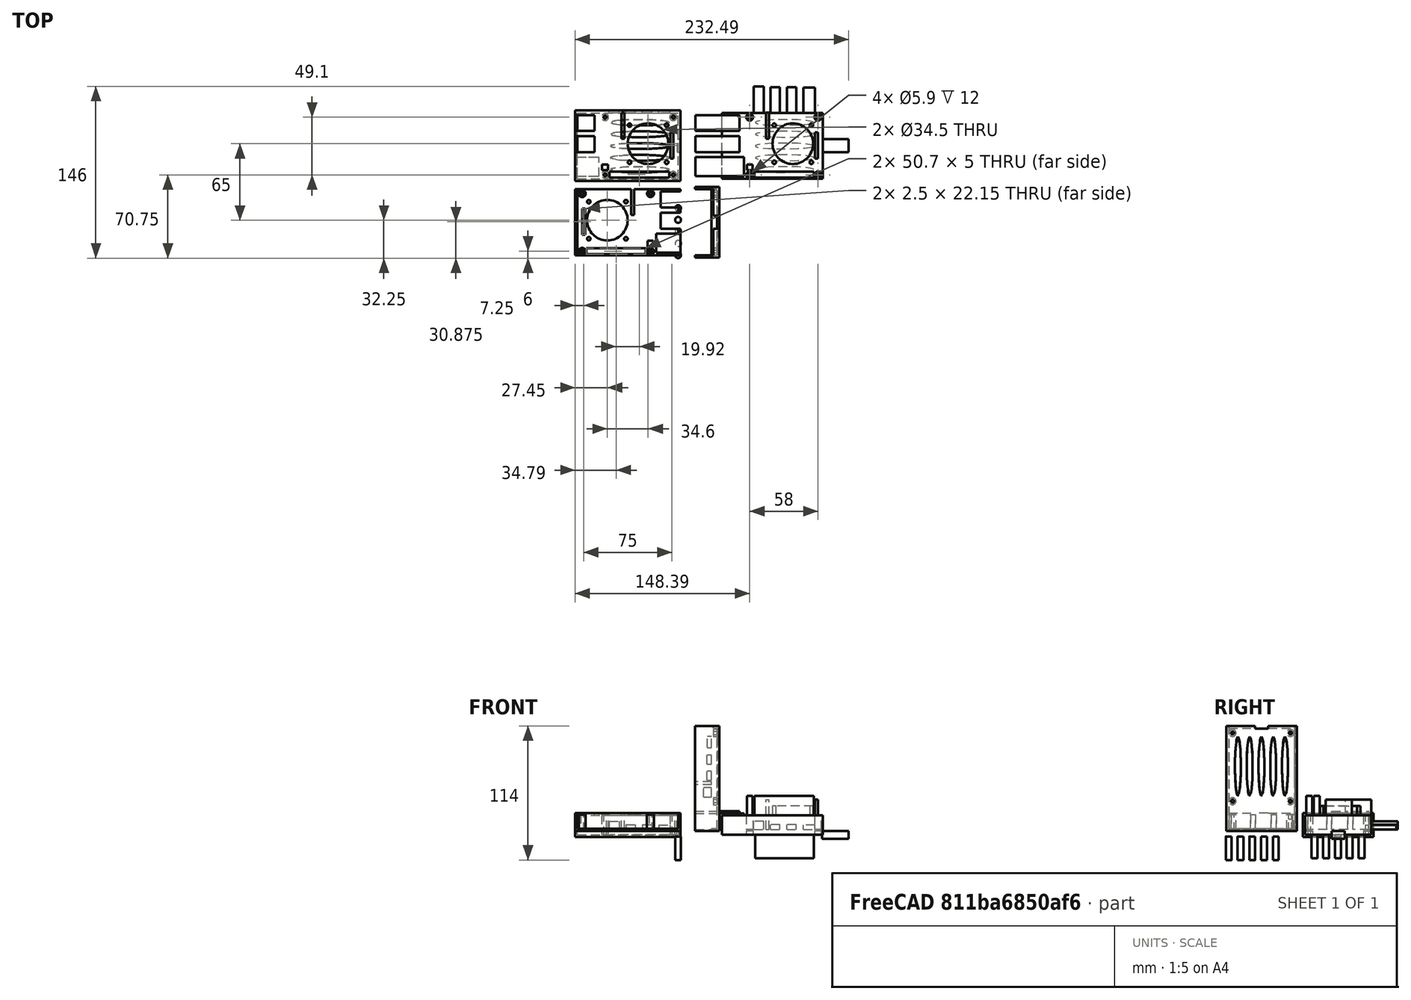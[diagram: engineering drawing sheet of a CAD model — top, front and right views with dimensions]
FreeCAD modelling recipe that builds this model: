
FCSTD DOCUMENT  (FreeCAD 0.21R33771 (Git))
Label: rpi_case_csg
License: All rights reserved
LicenseURL: http://en.wikipedia.org/wiki/All_rights_reserved
objects: Part::Cylinder×84, Part::Box×75, Part::MultiFuse×19, Part::Cut×14, Part::Fuse×7, Part::Feature×4, Part::Common×1
note: 204 computed .brp shape members not serialized (recipe doc carries the construction recipe); baked Part::Feature solids carry a one-line shape summary decoded from their .brp

FEATURE [Part::Box] cube
  AttacherType = Attacher::AttachEngine3D
  Height = 20.5
  Length = 89.5
  Placement = pos=(-2,-2,-5) rot=(0,0,1;0rad)
  Width = 60
FEATURE [Part::Box] cube001
  AttacherType = Attacher::AttachEngine3D
  Height = 1.5
  Length = 85.5
  Placement = pos=(0,0,-1.5) rot=(0,0,1;0rad)
  Width = 56
FEATURE [Part::Box] cube002
  AttacherType = Attacher::AttachEngine3D
  Height = 13.6
  Length = 41.3
  Placement = pos=(-22.81,2.15,0) rot=(0,0,1;0rad)
  Width = 16.3
FEATURE [Part::Box] cube003
  AttacherType = Attacher::AttachEngine3D
  Height = 15.6
  Length = 37.44
  Placement = pos=(-22.81,22.6,0) rot=(0,0,1;0rad)
  Width = 13.5
FEATURE [Part::Box] cube004
  AttacherType = Attacher::AttachEngine3D
  Height = 15.6
  Length = 37.44
  Placement = pos=(-22.81,40.6,0) rot=(0,0,1;0rad)
  Width = 13.5
FEATURE [Part::Box] cube005
  AttacherType = Attacher::AttachEngine3D
  Height = 28.6
  Length = 50.7
  Placement = pos=(27.36,1,0) rot=(0,0,1;0rad)
  Width = 5
FEATURE [Part::Box] cube006
  AttacherType = Attacher::AttachEngine3D
  Height = 28.6
  Length = 5
  Placement = pos=(21,7.15,0) rot=(0,0,1;0rad)
  Width = 5
FEATURE [Part::Box] cube007
  AttacherType = Attacher::AttachEngine3D
  Height = 2.5
  Length = 15
  Placement = pos=(48,16.3,0) rot=(0,0,1;0rad)
  Width = 15
FEATURE [Part::Box] cube008
  AttacherType = Attacher::AttachEngine3D
  Height = 1.8
  Length = 10.8
  Placement = pos=(67.5,6.8,0) rot=(0,0,1;0rad)
  Width = 13.1
FEATURE [Part::Box] cube009
  AttacherType = Attacher::AttachEngine3D
  Height = 25.4
  Length = 2.5
  Placement = pos=(79,17.3,0) rot=(0,0,1;0rad)
  Width = 22.15
FEATURE [Part::Box] cube010
  AttacherType = Attacher::AttachEngine3D
  Height = 3.6
  Length = 9.7
  Placement = pos=(69.1,50,0) rot=(0,0,1;0rad)
  Width = 27.4
FEATURE [Part::Box] cube011
  AttacherType = Attacher::AttachEngine3D
  Height = 3.9
  Length = 7.95
  Placement = pos=(55,50,0) rot=(0,0,1;0rad)
  Width = 27.8
FEATURE [Part::Box] cube012
  AttacherType = Attacher::AttachEngine3D
  Height = 3.9
  Length = 7.95
  Placement = pos=(41.2,50,0) rot=(0,0,1;0rad)
  Width = 27.8
FEATURE [Part::Box] cube013
  AttacherType = Attacher::AttachEngine3D
  Height = 25.4
  Length = 2.5
  Placement = pos=(37.4,34.1,0) rot=(0,0,1;0rad)
  Width = 22.15
FEATURE [Part::Box] cube014
  AttacherType = Attacher::AttachEngine3D
  Height = 6.9
  Length = 8.5
  Placement = pos=(26.9,43.55,0) rot=(0,0,1;0rad)
  Width = 34.95
FEATURE [Part::Box] cube015
  AttacherType = Attacher::AttachEngine3D
  Height = 6.5
  Length = 22.55
  Placement = pos=(85,22.4,-8) rot=(0,0,1;0rad)
  Width = 11.11
FEATURE [Part::Cylinder] cylinder
  Angle = 360
  AttacherType = Attacher::AttachEngine3D
  FirstAngle = 0
  Height = 20
  Placement = pos=(44.3,14,0) rot=(0,0,1;0rad)
  Radius = 1.5
  SecondAngle = 0
FEATURE [Part::Cylinder] cylinder001
  Angle = 360
  AttacherType = Attacher::AttachEngine3D
  FirstAngle = 0
  Height = 20
  Placement = pos=(44.3,45.5,0) rot=(0,0,1;0rad)
  Radius = 1.5
  SecondAngle = 0
FEATURE [Part::Cylinder] cylinder002
  Angle = 360
  AttacherType = Attacher::AttachEngine3D
  FirstAngle = 0
  Height = 20
  Placement = pos=(75.8,14,0) rot=(0,0,1;0rad)
  Radius = 1.5
  SecondAngle = 0
FEATURE [Part::Cylinder] cylinder003
  Angle = 360
  AttacherType = Attacher::AttachEngine3D
  FirstAngle = 0
  Height = 20
  Placement = pos=(75.8,45.5,0) rot=(0,0,1;0rad)
  Radius = 1.5
  SecondAngle = 0
FEATURE [Part::Cylinder] cylinder004
  Angle = 360
  AttacherType = Attacher::AttachEngine3D
  FirstAngle = 0
  Height = 20
  Placement = pos=(60.05,29.75,0) rot=(0,0,1;0rad)
  Radius = 17.25
  SecondAngle = 0
FEATURE [Part::Cylinder] cylinder005 .. cylinder009  x5 (patterned run collapsed; names and placements below)
  Angle = 360
  AttacherType = Attacher::AttachEngine3D
  FirstAngle = 0
  Height = 20
  Radius = 2.5
  SecondAngle = 0
  placements: 5 in arithmetic series — first pos=(0,0,-24.5) rot=(0,0,1;0rad), step (0,10,0), last pos=(0,40,-24.5) rot=(0,0,1;0rad)
FEATURE [Part::MultiFuse] Matrix_Union
  Shapes = -> [cylinder005,cylinder006,cylinder007,cylinder008,cylinder009]
FEATURE [Part::Feature] Matrix_Deformation
  Placement = pos=(53,7.8,0) rot=(0,0,1;0rad)
  shape: bbox 75 x 48.66 x 20 mm, 15 faces, 5 solids (baked)
FEATURE [Part::Box] cube016
  AttacherType = Attacher::AttachEngine3D
  Height = 12
  Length = 85.5
  Width = 56
FEATURE [Part::Box] cube017
  AttacherType = Attacher::AttachEngine3D
  Height = 3
  Length = 85.5
  Placement = pos=(0,0,-4.5) rot=(0,0,1;0rad)
  Width = 56
FEATURE [Part::Fuse] union
  Base = -> cube016
  Tool = -> cube017
FEATURE [Part::Cylinder] cylinder010
  Angle = 360
  AttacherType = Attacher::AttachEngine3D
  FirstAngle = 0
  Height = 22
  Placement = pos=(22.2,2,-11) rot=(0,0,1;0rad)
  Radius = 2.95
  SecondAngle = 0
FEATURE [Part::Cylinder] cylinder011
  Angle = 360
  AttacherType = Attacher::AttachEngine3D
  FirstAngle = 0
  Height = 22
  Placement = pos=(22.2,51.1,-11) rot=(0,0,1;0rad)
  Radius = 2.95
  SecondAngle = 0
FEATURE [Part::Cylinder] cylinder012
  Angle = 360
  AttacherType = Attacher::AttachEngine3D
  FirstAngle = 0
  Height = 22
  Placement = pos=(80.2,2,-11) rot=(0,0,1;0rad)
  Radius = 2.95
  SecondAngle = 0
FEATURE [Part::Cylinder] cylinder013
  Angle = 360
  AttacherType = Attacher::AttachEngine3D
  FirstAngle = 0
  Height = 22
  Placement = pos=(80.2,51.1,-11) rot=(0,0,1;0rad)
  Radius = 2.95
  SecondAngle = 0
FEATURE [Part::MultiFuse] Matrix_Union001
  Placement = pos=(1.25,1.25,4.5) rot=(0,0,1;0rad)
  Shapes = -> [cylinder010,cylinder011,cylinder012,cylinder013]
FEATURE [Part::Cut] difference
  Base = -> union
  Tool = -> Matrix_Union001
FEATURE [Part::MultiFuse] Matrix_Union002
  Placement = pos=(0,0,1.5) rot=(0,0,1;0rad)
  Shapes = -> [cube001,cube002,cube003,cube004,cube005,cube006,cube007,cube008,cube009,cube010,cube011,cube012,cube013,cube014,cube015,cylinder,cylinder001,cylinder002,cylinder003,cylinder004,Matrix_Deformation,difference]
FEATURE [Part::Cylinder] cylinder014
  Angle = 360
  AttacherType = Attacher::AttachEngine3D
  FirstAngle = 0
  Height = 22
  Placement = pos=(22.2,2,-11) rot=(0,0,1;0rad)
  Radius = 1.25
  SecondAngle = 0
FEATURE [Part::Cylinder] cylinder015
  Angle = 360
  AttacherType = Attacher::AttachEngine3D
  FirstAngle = 0
  Height = 22
  Placement = pos=(22.2,51.1,-11) rot=(0,0,1;0rad)
  Radius = 1.25
  SecondAngle = 0
FEATURE [Part::Cylinder] cylinder016
  Angle = 360
  AttacherType = Attacher::AttachEngine3D
  FirstAngle = 0
  Height = 22
  Placement = pos=(80.2,2,-11) rot=(0,0,1;0rad)
  Radius = 1.25
  SecondAngle = 0
FEATURE [Part::Cylinder] cylinder017
  Angle = 360
  AttacherType = Attacher::AttachEngine3D
  FirstAngle = 0
  Height = 22
  Placement = pos=(80.2,51.1,-11) rot=(0,0,1;0rad)
  Radius = 1.25
  SecondAngle = 0
FEATURE [Part::MultiFuse] Matrix_Union003
  Placement = pos=(1.25,1.25,4.5) rot=(0,0,1;0rad)
  Shapes = -> [cylinder014,cylinder015,cylinder016,cylinder017]
FEATURE [Part::Cut] difference001
  Base = -> Matrix_Union002
  Tool = -> Matrix_Union003
FEATURE [Part::Cylinder] cylinder018
  Angle = 360
  AttacherType = Attacher::AttachEngine3D
  FirstAngle = 0
  Height = 22
  Placement = pos=(22.2,2,-11) rot=(0,0,1;0rad)
  Radius = 1.25
  SecondAngle = 0
FEATURE [Part::Cylinder] cylinder019
  Angle = 360
  AttacherType = Attacher::AttachEngine3D
  FirstAngle = 0
  Height = 22
  Placement = pos=(22.2,51.1,-11) rot=(0,0,1;0rad)
  Radius = 1.25
  SecondAngle = 0
FEATURE [Part::Cylinder] cylinder020
  Angle = 360
  AttacherType = Attacher::AttachEngine3D
  FirstAngle = 0
  Height = 22
  Placement = pos=(80.2,2,-11) rot=(0,0,1;0rad)
  Radius = 1.25
  SecondAngle = 0
FEATURE [Part::Cylinder] cylinder021
  Angle = 360
  AttacherType = Attacher::AttachEngine3D
  FirstAngle = 0
  Height = 22
  Placement = pos=(80.2,51.1,-11) rot=(0,0,1;0rad)
  Radius = 1.25
  SecondAngle = 0
FEATURE [Part::MultiFuse] Matrix_Union004
  Placement = pos=(1.25,1.25,4.5) rot=(0,0,1;0rad)
  Shapes = -> [cylinder018,cylinder019,cylinder020,cylinder021]
FEATURE [Part::Fuse] union001
  Base = -> difference001
  Tool = -> Matrix_Union004
FEATURE [Part::Cut] difference002
  Base = -> cube
  Tool = -> union001
FEATURE [Part::Box] cube018
  AttacherType = Attacher::AttachEngine3D
  Height = 17
  Length = 89.5
  Placement = pos=(-2,0,0) rot=(0,0,1;0rad)
  Width = 56
FEATURE [Part::Box] cube019
  AttacherType = Attacher::AttachEngine3D
  Height = 1.5
  Length = 2
  Placement = pos=(-2,0,0) rot=(0,0,1;0rad)
  Width = 56
FEATURE [Part::Cut] difference003
  Base = -> cube018
  Tool = -> cube019
FEATURE [Part::Common] intersection
  Base = -> difference002
  Placement = pos=(0,0,15.5) rot=(0,1,0;3.14159rad)
  Tool = -> difference003
FEATURE [Part::Box] cube020
  AttacherType = Attacher::AttachEngine3D
  Height = 20.5
  Length = 89.5
  Placement = pos=(-2,-2,-5) rot=(0,0,1;0rad)
  Width = 60
FEATURE [Part::Box] cube021
  AttacherType = Attacher::AttachEngine3D
  Height = 1.5
  Length = 85.5
  Placement = pos=(0,0,-1.5) rot=(0,0,1;0rad)
  Width = 56
FEATURE [Part::Box] cube022
  AttacherType = Attacher::AttachEngine3D
  Height = 13.6
  Length = 41.3
  Placement = pos=(-22.81,2.15,0) rot=(0,0,1;0rad)
  Width = 16.3
FEATURE [Part::Box] cube023
  AttacherType = Attacher::AttachEngine3D
  Height = 15.6
  Length = 37.44
  Placement = pos=(-22.81,22.6,0) rot=(0,0,1;0rad)
  Width = 13.5
FEATURE [Part::Box] cube024
  AttacherType = Attacher::AttachEngine3D
  Height = 15.6
  Length = 37.44
  Placement = pos=(-22.81,40.6,0) rot=(0,0,1;0rad)
  Width = 13.5
FEATURE [Part::Box] cube025
  AttacherType = Attacher::AttachEngine3D
  Height = 28.6
  Length = 50.7
  Placement = pos=(27.36,1,0) rot=(0,0,1;0rad)
  Width = 5
FEATURE [Part::Box] cube026
  AttacherType = Attacher::AttachEngine3D
  Height = 28.6
  Length = 5
  Placement = pos=(21,7.15,0) rot=(0,0,1;0rad)
  Width = 5
FEATURE [Part::Box] cube027
  AttacherType = Attacher::AttachEngine3D
  Height = 2.5
  Length = 15
  Placement = pos=(48,16.3,0) rot=(0,0,1;0rad)
  Width = 15
FEATURE [Part::Box] cube028
  AttacherType = Attacher::AttachEngine3D
  Height = 1.8
  Length = 10.8
  Placement = pos=(67.5,6.8,0) rot=(0,0,1;0rad)
  Width = 13.1
FEATURE [Part::Box] cube029
  AttacherType = Attacher::AttachEngine3D
  Height = 25.4
  Length = 2.5
  Placement = pos=(79,17.3,0) rot=(0,0,1;0rad)
  Width = 22.15
FEATURE [Part::Box] cube030
  AttacherType = Attacher::AttachEngine3D
  Height = 3.6
  Length = 9.7
  Placement = pos=(69.1,50,0) rot=(0,0,1;0rad)
  Width = 27.4
FEATURE [Part::Box] cube031
  AttacherType = Attacher::AttachEngine3D
  Height = 3.9
  Length = 7.95
  Placement = pos=(55,50,0) rot=(0,0,1;0rad)
  Width = 27.8
FEATURE [Part::Box] cube032
  AttacherType = Attacher::AttachEngine3D
  Height = 3.9
  Length = 7.95
  Placement = pos=(41.2,50,0) rot=(0,0,1;0rad)
  Width = 27.8
FEATURE [Part::Box] cube033
  AttacherType = Attacher::AttachEngine3D
  Height = 25.4
  Length = 2.5
  Placement = pos=(37.4,34.1,0) rot=(0,0,1;0rad)
  Width = 22.15
FEATURE [Part::Box] cube034
  AttacherType = Attacher::AttachEngine3D
  Height = 6.9
  Length = 8.5
  Placement = pos=(26.9,43.55,0) rot=(0,0,1;0rad)
  Width = 34.95
FEATURE [Part::Box] cube035
  AttacherType = Attacher::AttachEngine3D
  Height = 6.5
  Length = 22.55
  Placement = pos=(85,22.4,-8) rot=(0,0,1;0rad)
  Width = 11.11
FEATURE [Part::Cylinder] cylinder022
  Angle = 360
  AttacherType = Attacher::AttachEngine3D
  FirstAngle = 0
  Height = 20
  Placement = pos=(44.3,14,0) rot=(0,0,1;0rad)
  Radius = 1.5
  SecondAngle = 0
FEATURE [Part::Cylinder] cylinder023
  Angle = 360
  AttacherType = Attacher::AttachEngine3D
  FirstAngle = 0
  Height = 20
  Placement = pos=(44.3,45.5,0) rot=(0,0,1;0rad)
  Radius = 1.5
  SecondAngle = 0
FEATURE [Part::Cylinder] cylinder024
  Angle = 360
  AttacherType = Attacher::AttachEngine3D
  FirstAngle = 0
  Height = 20
  Placement = pos=(75.8,14,0) rot=(0,0,1;0rad)
  Radius = 1.5
  SecondAngle = 0
FEATURE [Part::Cylinder] cylinder025
  Angle = 360
  AttacherType = Attacher::AttachEngine3D
  FirstAngle = 0
  Height = 20
  Placement = pos=(75.8,45.5,0) rot=(0,0,1;0rad)
  Radius = 1.5
  SecondAngle = 0
FEATURE [Part::Cylinder] cylinder026
  Angle = 360
  AttacherType = Attacher::AttachEngine3D
  FirstAngle = 0
  Height = 20
  Placement = pos=(60.05,29.75,0) rot=(0,0,1;0rad)
  Radius = 17.25
  SecondAngle = 0
FEATURE [Part::Cylinder] cylinder027 .. cylinder031  x5 (patterned run collapsed; names and placements below)
  Angle = 360
  AttacherType = Attacher::AttachEngine3D
  FirstAngle = 0
  Height = 20
  Radius = 2.5
  SecondAngle = 0
  placements: 5 in arithmetic series — first pos=(0,0,-24.5) rot=(0,0,1;0rad), step (0,10,0), last pos=(0,40,-24.5) rot=(0,0,1;0rad)
FEATURE [Part::MultiFuse] Matrix_Union005
  Shapes = -> [cylinder027,cylinder028,cylinder029,cylinder030,cylinder031]
FEATURE [Part::Feature] Matrix_Deformation001
  Placement = pos=(53,7.8,0) rot=(0,0,1;0rad)
  shape: bbox 75 x 48.66 x 20 mm, 15 faces, 5 solids (baked)
FEATURE [Part::Box] cube036
  AttacherType = Attacher::AttachEngine3D
  Height = 12
  Length = 85.5
  Width = 56
FEATURE [Part::Box] cube037
  AttacherType = Attacher::AttachEngine3D
  Height = 3
  Length = 85.5
  Placement = pos=(0,0,-4.5) rot=(0,0,1;0rad)
  Width = 56
FEATURE [Part::Fuse] union002
  Base = -> cube036
  Tool = -> cube037
FEATURE [Part::Cylinder] cylinder032
  Angle = 360
  AttacherType = Attacher::AttachEngine3D
  FirstAngle = 0
  Height = 22
  Placement = pos=(22.2,2,-11) rot=(0,0,1;0rad)
  Radius = 2.95
  SecondAngle = 0
FEATURE [Part::Cylinder] cylinder033
  Angle = 360
  AttacherType = Attacher::AttachEngine3D
  FirstAngle = 0
  Height = 22
  Placement = pos=(22.2,51.1,-11) rot=(0,0,1;0rad)
  Radius = 2.95
  SecondAngle = 0
FEATURE [Part::Cylinder] cylinder034
  Angle = 360
  AttacherType = Attacher::AttachEngine3D
  FirstAngle = 0
  Height = 22
  Placement = pos=(80.2,2,-11) rot=(0,0,1;0rad)
  Radius = 2.95
  SecondAngle = 0
FEATURE [Part::Cylinder] cylinder035
  Angle = 360
  AttacherType = Attacher::AttachEngine3D
  FirstAngle = 0
  Height = 22
  Placement = pos=(80.2,51.1,-11) rot=(0,0,1;0rad)
  Radius = 2.95
  SecondAngle = 0
FEATURE [Part::MultiFuse] Matrix_Union006
  Placement = pos=(1.25,1.25,4.5) rot=(0,0,1;0rad)
  Shapes = -> [cylinder032,cylinder033,cylinder034,cylinder035]
FEATURE [Part::Cut] difference004
  Base = -> union002
  Tool = -> Matrix_Union006
FEATURE [Part::MultiFuse] Matrix_Union007
  Placement = pos=(0,0,1.5) rot=(0,0,1;0rad)
  Shapes = -> [cube021,cube022,cube023,cube024,cube025,cube026,cube027,cube028,cube029,cube030,cube031,cube032,cube033,cube034,cube035,cylinder022,cylinder023,cylinder024,cylinder025,cylinder026,Matrix_Deformation001,difference004]
FEATURE [Part::Cylinder] cylinder036
  Angle = 360
  AttacherType = Attacher::AttachEngine3D
  FirstAngle = 0
  Height = 22
  Placement = pos=(22.2,2,-11) rot=(0,0,1;0rad)
  Radius = 1.25
  SecondAngle = 0
FEATURE [Part::Cylinder] cylinder037
  Angle = 360
  AttacherType = Attacher::AttachEngine3D
  FirstAngle = 0
  Height = 22
  Placement = pos=(22.2,51.1,-11) rot=(0,0,1;0rad)
  Radius = 1.25
  SecondAngle = 0
FEATURE [Part::Cylinder] cylinder038
  Angle = 360
  AttacherType = Attacher::AttachEngine3D
  FirstAngle = 0
  Height = 22
  Placement = pos=(80.2,2,-11) rot=(0,0,1;0rad)
  Radius = 1.25
  SecondAngle = 0
FEATURE [Part::Cylinder] cylinder039
  Angle = 360
  AttacherType = Attacher::AttachEngine3D
  FirstAngle = 0
  Height = 22
  Placement = pos=(80.2,51.1,-11) rot=(0,0,1;0rad)
  Radius = 1.25
  SecondAngle = 0
FEATURE [Part::MultiFuse] Matrix_Union008
  Placement = pos=(1.25,1.25,4.5) rot=(0,0,1;0rad)
  Shapes = -> [cylinder036,cylinder037,cylinder038,cylinder039]
FEATURE [Part::Cut] difference005
  Base = -> Matrix_Union007
  Tool = -> Matrix_Union008
FEATURE [Part::Cylinder] cylinder040
  Angle = 360
  AttacherType = Attacher::AttachEngine3D
  FirstAngle = 0
  Height = 22
  Placement = pos=(22.2,2,-11) rot=(0,0,1;0rad)
  Radius = 1.25
  SecondAngle = 0
FEATURE [Part::Cylinder] cylinder041
  Angle = 360
  AttacherType = Attacher::AttachEngine3D
  FirstAngle = 0
  Height = 22
  Placement = pos=(22.2,51.1,-11) rot=(0,0,1;0rad)
  Radius = 1.25
  SecondAngle = 0
FEATURE [Part::Cylinder] cylinder042
  Angle = 360
  AttacherType = Attacher::AttachEngine3D
  FirstAngle = 0
  Height = 22
  Placement = pos=(80.2,2,-11) rot=(0,0,1;0rad)
  Radius = 1.25
  SecondAngle = 0
FEATURE [Part::Cylinder] cylinder043
  Angle = 360
  AttacherType = Attacher::AttachEngine3D
  FirstAngle = 0
  Height = 22
  Placement = pos=(80.2,51.1,-11) rot=(0,0,1;0rad)
  Radius = 1.25
  SecondAngle = 0
FEATURE [Part::MultiFuse] Matrix_Union009
  Placement = pos=(1.25,1.25,4.5) rot=(0,0,1;0rad)
  Shapes = -> [cylinder040,cylinder041,cylinder042,cylinder043]
FEATURE [Part::Fuse] union003
  Base = -> difference005
  Tool = -> Matrix_Union009
FEATURE [Part::Cut] difference006
  Base = -> cube020
  Tool = -> union003
FEATURE [Part::Box] cube038
  AttacherType = Attacher::AttachEngine3D
  Height = 17
  Length = 89.5
  Placement = pos=(-2,0,0) rot=(0,0,1;0rad)
  Width = 56
FEATURE [Part::Box] cube039
  AttacherType = Attacher::AttachEngine3D
  Height = 1.5
  Length = 2
  Placement = pos=(-2,0,0) rot=(0,0,1;0rad)
  Width = 56
FEATURE [Part::Cut] difference007
  Base = -> cube038
  Tool = -> cube039
FEATURE [Part::Cut] difference008
  Base = -> difference006
  Placement = pos=(30,0,2) rot=(0,-1,0;1.5708rad)
  Tool = -> difference007
FEATURE [Part::Box] cube040
  AttacherType = Attacher::AttachEngine3D
  Height = 20.5
  Length = 89.5
  Placement = pos=(-2,-2,-5) rot=(0,0,1;0rad)
  Width = 60
FEATURE [Part::Box] cube041
  AttacherType = Attacher::AttachEngine3D
  Height = 1.5
  Length = 85.5
  Placement = pos=(0,0,-1.5) rot=(0,0,1;0rad)
  Width = 56
FEATURE [Part::Box] cube042
  AttacherType = Attacher::AttachEngine3D
  Height = 13.6
  Length = 41.3
  Placement = pos=(-22.81,2.15,0) rot=(0,0,1;0rad)
  Width = 16.3
FEATURE [Part::Box] cube043
  AttacherType = Attacher::AttachEngine3D
  Height = 15.6
  Length = 37.44
  Placement = pos=(-22.81,22.6,0) rot=(0,0,1;0rad)
  Width = 13.5
FEATURE [Part::Box] cube044
  AttacherType = Attacher::AttachEngine3D
  Height = 15.6
  Length = 37.44
  Placement = pos=(-22.81,40.6,0) rot=(0,0,1;0rad)
  Width = 13.5
FEATURE [Part::Box] cube045
  AttacherType = Attacher::AttachEngine3D
  Height = 28.6
  Length = 50.7
  Placement = pos=(27.36,1,0) rot=(0,0,1;0rad)
  Width = 5
FEATURE [Part::Box] cube046
  AttacherType = Attacher::AttachEngine3D
  Height = 28.6
  Length = 5
  Placement = pos=(21,7.15,0) rot=(0,0,1;0rad)
  Width = 5
FEATURE [Part::Box] cube047
  AttacherType = Attacher::AttachEngine3D
  Height = 2.5
  Length = 15
  Placement = pos=(48,16.3,0) rot=(0,0,1;0rad)
  Width = 15
FEATURE [Part::Box] cube048
  AttacherType = Attacher::AttachEngine3D
  Height = 1.8
  Length = 10.8
  Placement = pos=(67.5,6.8,0) rot=(0,0,1;0rad)
  Width = 13.1
FEATURE [Part::Box] cube049
  AttacherType = Attacher::AttachEngine3D
  Height = 25.4
  Length = 2.5
  Placement = pos=(79,17.3,0) rot=(0,0,1;0rad)
  Width = 22.15
FEATURE [Part::Box] cube050
  AttacherType = Attacher::AttachEngine3D
  Height = 3.6
  Length = 9.7
  Placement = pos=(69.1,50,0) rot=(0,0,1;0rad)
  Width = 27.4
FEATURE [Part::Box] cube051
  AttacherType = Attacher::AttachEngine3D
  Height = 3.9
  Length = 7.95
  Placement = pos=(55,50,0) rot=(0,0,1;0rad)
  Width = 27.8
FEATURE [Part::Box] cube052
  AttacherType = Attacher::AttachEngine3D
  Height = 3.9
  Length = 7.95
  Placement = pos=(41.2,50,0) rot=(0,0,1;0rad)
  Width = 27.8
FEATURE [Part::Box] cube053
  AttacherType = Attacher::AttachEngine3D
  Height = 25.4
  Length = 2.5
  Placement = pos=(37.4,34.1,0) rot=(0,0,1;0rad)
  Width = 22.15
FEATURE [Part::Box] cube054
  AttacherType = Attacher::AttachEngine3D
  Height = 6.9
  Length = 8.5
  Placement = pos=(26.9,43.55,0) rot=(0,0,1;0rad)
  Width = 34.95
FEATURE [Part::Box] cube055
  AttacherType = Attacher::AttachEngine3D
  Height = 6.5
  Length = 22.55
  Placement = pos=(85,22.4,-8) rot=(0,0,1;0rad)
  Width = 11.11
FEATURE [Part::Cylinder] cylinder044
  Angle = 360
  AttacherType = Attacher::AttachEngine3D
  FirstAngle = 0
  Height = 20
  Placement = pos=(44.3,14,0) rot=(0,0,1;0rad)
  Radius = 1.5
  SecondAngle = 0
FEATURE [Part::Cylinder] cylinder045
  Angle = 360
  AttacherType = Attacher::AttachEngine3D
  FirstAngle = 0
  Height = 20
  Placement = pos=(44.3,45.5,0) rot=(0,0,1;0rad)
  Radius = 1.5
  SecondAngle = 0
FEATURE [Part::Cylinder] cylinder046
  Angle = 360
  AttacherType = Attacher::AttachEngine3D
  FirstAngle = 0
  Height = 20
  Placement = pos=(75.8,14,0) rot=(0,0,1;0rad)
  Radius = 1.5
  SecondAngle = 0
FEATURE [Part::Cylinder] cylinder047
  Angle = 360
  AttacherType = Attacher::AttachEngine3D
  FirstAngle = 0
  Height = 20
  Placement = pos=(75.8,45.5,0) rot=(0,0,1;0rad)
  Radius = 1.5
  SecondAngle = 0
FEATURE [Part::Cylinder] cylinder048
  Angle = 360
  AttacherType = Attacher::AttachEngine3D
  FirstAngle = 0
  Height = 20
  Placement = pos=(60.05,29.75,0) rot=(0,0,1;0rad)
  Radius = 17.25
  SecondAngle = 0
FEATURE [Part::Cylinder] cylinder049 .. cylinder053  x5 (patterned run collapsed; names and placements below)
  Angle = 360
  AttacherType = Attacher::AttachEngine3D
  FirstAngle = 0
  Height = 20
  Radius = 2.5
  SecondAngle = 0
  placements: 5 in arithmetic series — first pos=(0,0,-24.5) rot=(0,0,1;0rad), step (0,10,0), last pos=(0,40,-24.5) rot=(0,0,1;0rad)
FEATURE [Part::MultiFuse] Matrix_Union010
  Shapes = -> [cylinder049,cylinder050,cylinder051,cylinder052,cylinder053]
FEATURE [Part::Feature] Matrix_Deformation002
  Placement = pos=(53,7.8,0) rot=(0,0,1;0rad)
  shape: bbox 75 x 48.66 x 20 mm, 15 faces, 5 solids (baked)
FEATURE [Part::Box] cube056
  AttacherType = Attacher::AttachEngine3D
  Height = 12
  Length = 85.5
  Width = 56
FEATURE [Part::Box] cube057
  AttacherType = Attacher::AttachEngine3D
  Height = 3
  Length = 85.5
  Placement = pos=(0,0,-4.5) rot=(0,0,1;0rad)
  Width = 56
FEATURE [Part::Fuse] union004
  Base = -> cube056
  Tool = -> cube057
FEATURE [Part::Cylinder] cylinder054
  Angle = 360
  AttacherType = Attacher::AttachEngine3D
  FirstAngle = 0
  Height = 22
  Placement = pos=(22.2,2,-11) rot=(0,0,1;0rad)
  Radius = 2.95
  SecondAngle = 0
FEATURE [Part::Cylinder] cylinder055
  Angle = 360
  AttacherType = Attacher::AttachEngine3D
  FirstAngle = 0
  Height = 22
  Placement = pos=(22.2,51.1,-11) rot=(0,0,1;0rad)
  Radius = 2.95
  SecondAngle = 0
FEATURE [Part::Cylinder] cylinder056
  Angle = 360
  AttacherType = Attacher::AttachEngine3D
  FirstAngle = 0
  Height = 22
  Placement = pos=(80.2,2,-11) rot=(0,0,1;0rad)
  Radius = 2.95
  SecondAngle = 0
FEATURE [Part::Cylinder] cylinder057
  Angle = 360
  AttacherType = Attacher::AttachEngine3D
  FirstAngle = 0
  Height = 22
  Placement = pos=(80.2,51.1,-11) rot=(0,0,1;0rad)
  Radius = 2.95
  SecondAngle = 0
FEATURE [Part::MultiFuse] Matrix_Union011
  Placement = pos=(1.25,1.25,4.5) rot=(0,0,1;0rad)
  Shapes = -> [cylinder054,cylinder055,cylinder056,cylinder057]
FEATURE [Part::Cut] difference009
  Base = -> union004
  Tool = -> Matrix_Union011
FEATURE [Part::MultiFuse] Matrix_Union012
  Placement = pos=(0,0,1.5) rot=(0,0,1;0rad)
  Shapes = -> [cube041,cube042,cube043,cube044,cube045,cube046,cube047,cube048,cube049,cube050,cube051,cube052,cube053,cube054,cube055,cylinder044,cylinder045,cylinder046,cylinder047,cylinder048,Matrix_Deformation002,difference009]
FEATURE [Part::Cylinder] cylinder058
  Angle = 360
  AttacherType = Attacher::AttachEngine3D
  FirstAngle = 0
  Height = 22
  Placement = pos=(22.2,2,-11) rot=(0,0,1;0rad)
  Radius = 1.25
  SecondAngle = 0
FEATURE [Part::Cylinder] cylinder059
  Angle = 360
  AttacherType = Attacher::AttachEngine3D
  FirstAngle = 0
  Height = 22
  Placement = pos=(22.2,51.1,-11) rot=(0,0,1;0rad)
  Radius = 1.25
  SecondAngle = 0
FEATURE [Part::Cylinder] cylinder060
  Angle = 360
  AttacherType = Attacher::AttachEngine3D
  FirstAngle = 0
  Height = 22
  Placement = pos=(80.2,2,-11) rot=(0,0,1;0rad)
  Radius = 1.25
  SecondAngle = 0
FEATURE [Part::Cylinder] cylinder061
  Angle = 360
  AttacherType = Attacher::AttachEngine3D
  FirstAngle = 0
  Height = 22
  Placement = pos=(80.2,51.1,-11) rot=(0,0,1;0rad)
  Radius = 1.25
  SecondAngle = 0
FEATURE [Part::MultiFuse] Matrix_Union013
  Placement = pos=(1.25,1.25,4.5) rot=(0,0,1;0rad)
  Shapes = -> [cylinder058,cylinder059,cylinder060,cylinder061]
FEATURE [Part::Cut] difference010
  Base = -> Matrix_Union012
  Tool = -> Matrix_Union013
FEATURE [Part::Cylinder] cylinder062
  Angle = 360
  AttacherType = Attacher::AttachEngine3D
  FirstAngle = 0
  Height = 22
  Placement = pos=(22.2,2,-11) rot=(0,0,1;0rad)
  Radius = 1.25
  SecondAngle = 0
FEATURE [Part::Cylinder] cylinder063
  Angle = 360
  AttacherType = Attacher::AttachEngine3D
  FirstAngle = 0
  Height = 22
  Placement = pos=(22.2,51.1,-11) rot=(0,0,1;0rad)
  Radius = 1.25
  SecondAngle = 0
FEATURE [Part::Cylinder] cylinder064
  Angle = 360
  AttacherType = Attacher::AttachEngine3D
  FirstAngle = 0
  Height = 22
  Placement = pos=(80.2,2,-11) rot=(0,0,1;0rad)
  Radius = 1.25
  SecondAngle = 0
FEATURE [Part::Cylinder] cylinder065
  Angle = 360
  AttacherType = Attacher::AttachEngine3D
  FirstAngle = 0
  Height = 22
  Placement = pos=(80.2,51.1,-11) rot=(0,0,1;0rad)
  Radius = 1.25
  SecondAngle = 0
FEATURE [Part::MultiFuse] Matrix_Union014
  Placement = pos=(1.25,1.25,4.5) rot=(0,0,1;0rad)
  Shapes = -> [cylinder062,cylinder063,cylinder064,cylinder065]
FEATURE [Part::Fuse] union005
  Base = -> difference010
  Tool = -> Matrix_Union014
FEATURE [Part::Cut] difference011
  Base = -> cube040
  Placement = pos=(-85.5,65,0) rot=(0,0,1;0rad)
  Tool = -> union005
FEATURE [Part::Box] cube058
  AttacherType = Attacher::AttachEngine3D
  Height = 1.5
  Length = 85.5
  Placement = pos=(0,0,-1.5) rot=(0,0,1;0rad)
  Width = 56
FEATURE [Part::Box] cube059
  AttacherType = Attacher::AttachEngine3D
  Height = 13.6
  Length = 41.3
  Placement = pos=(-22.81,2.15,0) rot=(0,0,1;0rad)
  Width = 16.3
FEATURE [Part::Box] cube060
  AttacherType = Attacher::AttachEngine3D
  Height = 15.6
  Length = 37.44
  Placement = pos=(-22.81,22.6,0) rot=(0,0,1;0rad)
  Width = 13.5
FEATURE [Part::Box] cube061
  AttacherType = Attacher::AttachEngine3D
  Height = 15.6
  Length = 37.44
  Placement = pos=(-22.81,40.6,0) rot=(0,0,1;0rad)
  Width = 13.5
FEATURE [Part::Box] cube062
  AttacherType = Attacher::AttachEngine3D
  Height = 28.6
  Length = 50.7
  Placement = pos=(27.36,1,0) rot=(0,0,1;0rad)
  Width = 5
FEATURE [Part::Box] cube063
  AttacherType = Attacher::AttachEngine3D
  Height = 28.6
  Length = 5
  Placement = pos=(21,7.15,0) rot=(0,0,1;0rad)
  Width = 5
FEATURE [Part::Box] cube064
  AttacherType = Attacher::AttachEngine3D
  Height = 2.5
  Length = 15
  Placement = pos=(48,16.3,0) rot=(0,0,1;0rad)
  Width = 15
FEATURE [Part::Box] cube065
  AttacherType = Attacher::AttachEngine3D
  Height = 1.8
  Length = 10.8
  Placement = pos=(67.5,6.8,0) rot=(0,0,1;0rad)
  Width = 13.1
FEATURE [Part::Box] cube066
  AttacherType = Attacher::AttachEngine3D
  Height = 25.4
  Length = 2.5
  Placement = pos=(79,17.3,0) rot=(0,0,1;0rad)
  Width = 22.15
FEATURE [Part::Box] cube067
  AttacherType = Attacher::AttachEngine3D
  Height = 3.6
  Length = 9.7
  Placement = pos=(69.1,50,0) rot=(0,0,1;0rad)
  Width = 27.4
FEATURE [Part::Box] cube068
  AttacherType = Attacher::AttachEngine3D
  Height = 3.9
  Length = 7.95
  Placement = pos=(55,50,0) rot=(0,0,1;0rad)
  Width = 27.8
FEATURE [Part::Box] cube069
  AttacherType = Attacher::AttachEngine3D
  Height = 3.9
  Length = 7.95
  Placement = pos=(41.2,50,0) rot=(0,0,1;0rad)
  Width = 27.8
FEATURE [Part::Box] cube070
  AttacherType = Attacher::AttachEngine3D
  Height = 25.4
  Length = 2.5
  Placement = pos=(37.4,34.1,0) rot=(0,0,1;0rad)
  Width = 22.15
FEATURE [Part::Box] cube071
  AttacherType = Attacher::AttachEngine3D
  Height = 6.9
  Length = 8.5
  Placement = pos=(26.9,43.55,0) rot=(0,0,1;0rad)
  Width = 34.95
FEATURE [Part::Box] cube072
  AttacherType = Attacher::AttachEngine3D
  Height = 6.5
  Length = 22.55
  Placement = pos=(85,22.4,-8) rot=(0,0,1;0rad)
  Width = 11.11
FEATURE [Part::Cylinder] cylinder066
  Angle = 360
  AttacherType = Attacher::AttachEngine3D
  FirstAngle = 0
  Height = 20
  Placement = pos=(44.3,14,0) rot=(0,0,1;0rad)
  Radius = 1.5
  SecondAngle = 0
FEATURE [Part::Cylinder] cylinder067
  Angle = 360
  AttacherType = Attacher::AttachEngine3D
  FirstAngle = 0
  Height = 20
  Placement = pos=(44.3,45.5,0) rot=(0,0,1;0rad)
  Radius = 1.5
  SecondAngle = 0
FEATURE [Part::Cylinder] cylinder068
  Angle = 360
  AttacherType = Attacher::AttachEngine3D
  FirstAngle = 0
  Height = 20
  Placement = pos=(75.8,14,0) rot=(0,0,1;0rad)
  Radius = 1.5
  SecondAngle = 0
FEATURE [Part::Cylinder] cylinder069
  Angle = 360
  AttacherType = Attacher::AttachEngine3D
  FirstAngle = 0
  Height = 20
  Placement = pos=(75.8,45.5,0) rot=(0,0,1;0rad)
  Radius = 1.5
  SecondAngle = 0
FEATURE [Part::Cylinder] cylinder070
  Angle = 360
  AttacherType = Attacher::AttachEngine3D
  FirstAngle = 0
  Height = 20
  Placement = pos=(60.05,29.75,0) rot=(0,0,1;0rad)
  Radius = 17.25
  SecondAngle = 0
FEATURE [Part::Cylinder] cylinder071 .. cylinder075  x5 (patterned run collapsed; names and placements below)
  Angle = 360
  AttacherType = Attacher::AttachEngine3D
  FirstAngle = 0
  Height = 20
  Radius = 2.5
  SecondAngle = 0
  placements: 5 in arithmetic series — first pos=(0,0,-24.5) rot=(0,0,1;0rad), step (0,10,0), last pos=(0,40,-24.5) rot=(0,0,1;0rad)
FEATURE [Part::MultiFuse] Matrix_Union015
  Shapes = -> [cylinder071,cylinder072,cylinder073,cylinder074,cylinder075]
FEATURE [Part::Feature] Matrix_Deformation003
  Placement = pos=(53,7.8,0) rot=(0,0,1;0rad)
  shape: bbox 75 x 48.66 x 20 mm, 15 faces, 5 solids (baked)
FEATURE [Part::Box] cube073
  AttacherType = Attacher::AttachEngine3D
  Height = 12
  Length = 85.5
  Width = 56
FEATURE [Part::Box] cube074
  AttacherType = Attacher::AttachEngine3D
  Height = 3
  Length = 85.5
  Placement = pos=(0,0,-4.5) rot=(0,0,1;0rad)
  Width = 56
FEATURE [Part::Fuse] union006
  Base = -> cube073
  Tool = -> cube074
FEATURE [Part::Cylinder] cylinder076
  Angle = 360
  AttacherType = Attacher::AttachEngine3D
  FirstAngle = 0
  Height = 22
  Placement = pos=(22.2,2,-11) rot=(0,0,1;0rad)
  Radius = 2.95
  SecondAngle = 0
FEATURE [Part::Cylinder] cylinder077
  Angle = 360
  AttacherType = Attacher::AttachEngine3D
  FirstAngle = 0
  Height = 22
  Placement = pos=(22.2,51.1,-11) rot=(0,0,1;0rad)
  Radius = 2.95
  SecondAngle = 0
FEATURE [Part::Cylinder] cylinder078
  Angle = 360
  AttacherType = Attacher::AttachEngine3D
  FirstAngle = 0
  Height = 22
  Placement = pos=(80.2,2,-11) rot=(0,0,1;0rad)
  Radius = 2.95
  SecondAngle = 0
FEATURE [Part::Cylinder] cylinder079
  Angle = 360
  AttacherType = Attacher::AttachEngine3D
  FirstAngle = 0
  Height = 22
  Placement = pos=(80.2,51.1,-11) rot=(0,0,1;0rad)
  Radius = 2.95
  SecondAngle = 0
FEATURE [Part::MultiFuse] Matrix_Union016
  Placement = pos=(1.25,1.25,4.5) rot=(0,0,1;0rad)
  Shapes = -> [cylinder076,cylinder077,cylinder078,cylinder079]
FEATURE [Part::Cut] difference012
  Base = -> union006
  Tool = -> Matrix_Union016
FEATURE [Part::MultiFuse] Matrix_Union017
  Placement = pos=(0,0,1.5) rot=(0,0,1;0rad)
  Shapes = -> [cube058,cube059,cube060,cube061,cube062,cube063,cube064,cube065,cube066,cube067,cube068,cube069,cube070,cube071,cube072,cylinder066,cylinder067,cylinder068,cylinder069,cylinder070,Matrix_Deformation003,difference012]
FEATURE [Part::Cylinder] cylinder080
  Angle = 360
  AttacherType = Attacher::AttachEngine3D
  FirstAngle = 0
  Height = 22
  Placement = pos=(22.2,2,-11) rot=(0,0,1;0rad)
  Radius = 1.25
  SecondAngle = 0
FEATURE [Part::Cylinder] cylinder081
  Angle = 360
  AttacherType = Attacher::AttachEngine3D
  FirstAngle = 0
  Height = 22
  Placement = pos=(22.2,51.1,-11) rot=(0,0,1;0rad)
  Radius = 1.25
  SecondAngle = 0
FEATURE [Part::Cylinder] cylinder082
  Angle = 360
  AttacherType = Attacher::AttachEngine3D
  FirstAngle = 0
  Height = 22
  Placement = pos=(80.2,2,-11) rot=(0,0,1;0rad)
  Radius = 1.25
  SecondAngle = 0
FEATURE [Part::Cylinder] cylinder083
  Angle = 360
  AttacherType = Attacher::AttachEngine3D
  FirstAngle = 0
  Height = 22
  Placement = pos=(80.2,51.1,-11) rot=(0,0,1;0rad)
  Radius = 1.25
  SecondAngle = 0
FEATURE [Part::MultiFuse] Matrix_Union018
  Placement = pos=(1.25,1.25,4.5) rot=(0,0,1;0rad)
  Shapes = -> [cylinder080,cylinder081,cylinder082,cylinder083]
FEATURE [Part::Cut] difference013
  Base = -> Matrix_Union017
  Placement = pos=(37.44,65,0) rot=(0,0,1;0rad)
  Tool = -> Matrix_Union018
